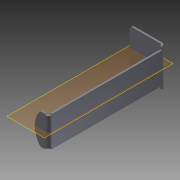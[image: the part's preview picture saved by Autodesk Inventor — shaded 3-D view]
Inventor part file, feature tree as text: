
AUTODESK INVENTOR PART (.ipt)
format: ipt  version: 2015 (Build 190159000, 159)  size: 209,408 bytes
history: native  units: mm
features: extrude x6, fillet x3, mirror x1, reference x1, other x1
ambient origin geometry x8: Origin, YZ Plane, XZ Plane, XY Plane, X Axis, Y Axis, Z Axis, Center Point
bodies: Solid1 (feature_tree)
feature tree (12):
  extrude  "Extrusión1"  Depth=1.5mm
  fillet  "Empalme1"  Radius=30.0mm
  extrude  "Extrusión2"  Depth=33.0mm TaperAngle=0.0deg
  extrude  "Extrusión4"  Depth=1.5mm
  mirror  "Simetría2"
  fillet  "Empalme4"  Radius=1.5mm
  extrude  "Extrusión7"  Depth=1.5mm
  extrude  "Extrusión8"  Depth=15.0mm
  fillet  "Empalme5"  Radius=100.2mm
  extrude  "Extrusión6"  Depth=100.0mm TaperAngle=0.0deg
  reference  "Referencia3"
  other  "Definición1"
